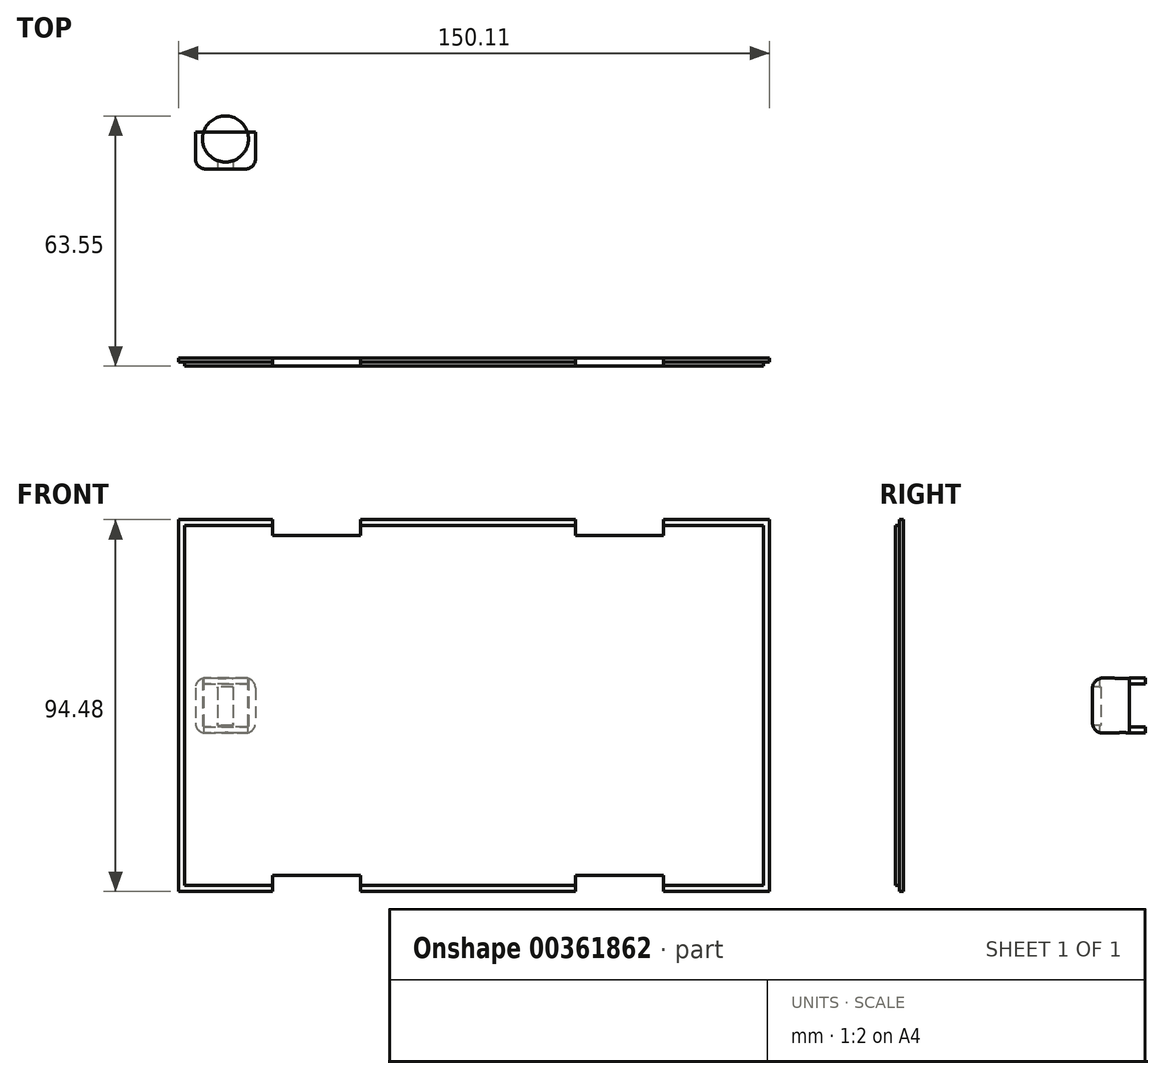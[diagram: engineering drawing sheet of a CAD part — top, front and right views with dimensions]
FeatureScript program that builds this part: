
annotation { "Feature Type Name" : "Feature", "Feature Type Description" : "" }
export const myFeature = defineFeature(function(context is Context, id is Id, definition is map)
    precondition{}
    {
        {
            var Q0;
            Q0=qCreatedBy(makeId("Front.planeOp"),FACE);
            var sketch = newSketch(context, id + "F0", { "sketchPlane" : qUnion([Q0])});
            skLineSegment(sketch, "E0", {"start": v(-53.36, 0) * mm, "end": v(-53.36, 45.72) * mm});
            skLineSegment(sketch, "E1", {"start": v(-53.36, 45.72) * mm, "end": v(-31, 45.72) * mm});
            skLineSegment(sketch, "E2", {"start": v(-31, 45.72) * mm, "end": v(-31, 43.18) * mm});
            skLineSegment(sketch, "E3", {"start": v(-31, 43.18) * mm, "end": v(-8.66, 43.18) * mm});
            skLineSegment(sketch, "E4", {"start": v(-8.66, 43.18) * mm, "end": v(-8.66, 45.72) * mm});
            skLineSegment(sketch, "E5", {"start": v(-8.66, 45.72) * mm, "end": v(45.95, 45.72) * mm});
            skLineSegment(sketch, "E6", {"start": v(45.95, 45.72) * mm, "end": v(45.95, 43.18) * mm});
            skLineSegment(sketch, "E7", {"start": v(45.95, 43.18) * mm, "end": v(68.3, 43.18) * mm});
            skLineSegment(sketch, "E8", {"start": v(68.3, 43.18) * mm, "end": v(68.3, 45.72) * mm});
            skLineSegment(sketch, "E9", {"start": v(68.3, 45.72) * mm, "end": v(93.7, 45.72) * mm});
            skLineSegment(sketch, "E10", {"start": v(93.7, 45.72) * mm, "end": v(93.7, 0) * mm});
            skLineSegment(sketch, "E11", {"start": v(93.7, 0) * mm, "end": v(-53.36, 0) * mm});
            skLineSegment(sketch, "E12.MirrorCS", {"start": v(-53.36, 0) * mm, "end": v(-53.36, -45.72) * mm});
            skLineSegment(sketch, "E13.MirrorCS", {"start": v(-53.36, -45.72) * mm, "end": v(-31, -45.72) * mm});
            skLineSegment(sketch, "E14.MirrorCS", {"start": v(-31, -45.72) * mm, "end": v(-31, -43.18) * mm});
            skLineSegment(sketch, "E15.MirrorCS", {"start": v(-31, -43.18) * mm, "end": v(-8.66, -43.18) * mm});
            skLineSegment(sketch, "E16.MirrorCS", {"start": v(-8.66, -43.18) * mm, "end": v(-8.66, -45.72) * mm});
            skLineSegment(sketch, "E17.MirrorCS", {"start": v(-8.66, -45.72) * mm, "end": v(45.95, -45.72) * mm});
            skLineSegment(sketch, "E18.MirrorCS", {"start": v(45.95, -45.72) * mm, "end": v(45.95, -43.18) * mm});
            skLineSegment(sketch, "E19.MirrorCS", {"start": v(45.95, -43.18) * mm, "end": v(68.3, -43.18) * mm});
            skLineSegment(sketch, "E20.MirrorCS", {"start": v(68.3, -43.18) * mm, "end": v(68.3, -45.72) * mm});
            skLineSegment(sketch, "E21.MirrorCS", {"start": v(68.3, -45.72) * mm, "end": v(93.7, -45.72) * mm});
            skLineSegment(sketch, "E22.MirrorCS", {"start": v(93.7, -45.72) * mm, "end": v(93.7, 0) * mm});
            skLineSegment(sketch, "E23.0", {"start": v(-54.88, 47.24) * mm, "end": v(-31, 47.24) * mm});
            skLineSegment(sketch, "E23.1", {"start": v(-54.88, 0) * mm, "end": v(-54.88, 47.24) * mm});
            skLineSegment(sketch, "E23.2", {"start": v(-54.88, 0) * mm, "end": v(-54.88, -47.24) * mm});
            skLineSegment(sketch, "E23.3", {"start": v(-54.88, -47.24) * mm, "end": v(-31, -47.24) * mm});
            skLineSegment(sketch, "E24", {"start": v(-31, 47.24) * mm, "end": v(-31, 45.72) * mm});
            skLineSegment(sketch, "E25", {"start": v(-31, -45.72) * mm, "end": v(-31, -47.24) * mm});
            skLineSegment(sketch, "E26", {"start": v(-8.66, 45.72) * mm, "end": v(-8.66, 47.24) * mm});
            skLineSegment(sketch, "E27", {"start": v(-8.66, 47.24) * mm, "end": v(45.95, 47.24) * mm});
            skLineSegment(sketch, "E28", {"start": v(45.95, 47.24) * mm, "end": v(45.95, 45.72) * mm});
            skLineSegment(sketch, "E29.0", {"start": v(68.3, -47.24) * mm, "end": v(95.23, -47.24) * mm});
            skLineSegment(sketch, "E29.1", {"start": v(95.23, -47.24) * mm, "end": v(95.23, 12.7) * mm});
            skLineSegment(sketch, "E29.2", {"start": v(95.23, 47.24) * mm, "end": v(95.23, 12.7) * mm});
            skLineSegment(sketch, "E29.3", {"start": v(68.3, 47.24) * mm, "end": v(95.23, 47.24) * mm});
            skLineSegment(sketch, "E30", {"start": v(68.3, 47.24) * mm, "end": v(68.3, 45.72) * mm});
            skLineSegment(sketch, "E31", {"start": v(68.3, -47.24) * mm, "end": v(68.3, -45.72) * mm});
            skLineSegment(sketch, "E32", {"start": v(-8.66, -45.72) * mm, "end": v(-8.66, -47.24) * mm});
            skLineSegment(sketch, "E33", {"start": v(-8.66, -47.24) * mm, "end": v(45.95, -47.24) * mm});
            skLineSegment(sketch, "E34", {"start": v(45.95, -47.24) * mm, "end": v(45.95, -45.72) * mm});
            skSolve(sketch);
        }
        {
            var Q0;
            Q0=makeQuery(id+"F0.imprint","IMPRINT",FACE,{"disambiguationData":[TD([[makeQuery(id+"F0.imprint","IMPRINT",EDGE,{"derivedFrom":sQuery(id+"F0.wireOp",EDGE,"E0")}),-1.0]])]});
            var Q1;
            Q1=makeQuery(id+"F0.imprint","IMPRINT",FACE,{"disambiguationData":[TD([[makeQuery(id+"F0.imprint","IMPRINT",EDGE,{"derivedFrom":sQuery(id+"F0.wireOp",EDGE,"E11")}),1.0]])]});
            extrude(context, id + "F1", {"entities" : qUnion([Q0, Q1]), "depth" : 2.03 * mm});
        }
        {
            var Q0;
            Q0=makeQuery(id+"F0.imprint","IMPRINT",FACE,{"disambiguationData":[TD([[makeQuery(id+"F0.imprint","IMPRINT",EDGE,{"derivedFrom":sQuery(id+"F0.wireOp",EDGE,"E0")}),1.0]])]});
            var Q1;
            Q1=makeQuery(id+"F0.imprint","IMPRINT",FACE,{"disambiguationData":[TD([[makeQuery(id+"F0.imprint","IMPRINT",EDGE,{"derivedFrom":sQuery(id+"F0.wireOp",EDGE,"E5")}),1.0]])]});
            var Q2;
            Q2=makeQuery(id+"F0.imprint","IMPRINT",FACE,{"disambiguationData":[TD([[makeQuery(id+"F0.imprint","IMPRINT",EDGE,{"derivedFrom":sQuery(id+"F0.wireOp",EDGE,"E9")}),1.0]])]});
            var Q3;
            Q3=makeQuery(id+"F0.imprint","IMPRINT",FACE,{"disambiguationData":[TD([[makeQuery(id+"F0.imprint","IMPRINT",EDGE,{"derivedFrom":sQuery(id+"F0.wireOp",EDGE,"E17.MirrorCS")}),-1.0]])]});
            extrude(context, id + "F2", {"entities" : qUnion([Q0, Q1, Q2, Q3]), "operationType" : NewBodyOperationType.ADD, "depth" : 1.02 * mm});
        }
        {
            var Q0;
            Q0=qCreatedBy(makeId("Top.planeOp"),FACE);
            var sketch = newSketch(context, id + "F3", { "sketchPlane" : qUnion([Q0])});
            skLineSegment(sketch, "E35.bottom", {"start": v(-50.6, 63.3) * mm, "end": v(-35.36, 63.3) * mm});
            skLineSegment(sketch, "E35.top", {"start": v(-50.6, 48.06) * mm, "end": v(-35.36, 48.06) * mm});
            skLineSegment(sketch, "E35.left", {"start": v(-50.6, 63.3) * mm, "end": v(-50.6, 48.06) * mm});
            skLineSegment(sketch, "E35.right", {"start": v(-35.36, 63.3) * mm, "end": v(-35.36, 48.06) * mm});
            skPoint(sketch, "E35.middle", {"position": v(-42.98, 55.68) * mm});
            skCircle(sketch, "E36", {"center": v(-42.98, 55.68) * mm, "radius": 5.84 * mm});
            skLineSegment(sketch, "E37", {"start": v(-50.6, 57.43) * mm, "end": v(-35.36, 57.43) * mm});
            skSolve(sketch);
        }
        {
            var Q0;
            {var subQ5=sQuery(id+"F3.wireOp",EDGE,"E35.top");Q0=makeQuery(id+"F3.imprint","IMPRINT",FACE,{"disambiguationData":[TD([[makeQuery(id+"F3.imprint","IMPRINT",EDGE,{"derivedFrom":subQ5}),1.0]])]});}
            var Q1;
            {var subQ0=sQuery(id+"F3.wireOp",EDGE,"E37");var subQ1=sQuery(id+"F3.wireOp",EDGE,"E36");var subQ2=makeQuery(id+"F3.imprint","INTERSECT",VERTEX,{"disambiguationData":[OD(0.0)],"derivedFrom":[subQ1,subQ0]});Q1=makeQuery(id+"F3.imprint","IMPRINT",FACE,{"disambiguationData":[TD([[makeQuery(id+"F3.imprint","IMPRINT",EDGE,{"disambiguationData":[TD([[subQ2,-1.0]])],"derivedFrom":subQ1}),1.0]])]});}
            extrude(context, id + "F4", {"entities" : qUnion([Q0, Q1]), "endBound" : BoundingType.SYMMETRIC, "depth" : 13.97 * mm});
        }
        {
            var Q0;
            {var subQ0=sQuery(id+"F3.wireOp",EDGE,"E37");var subQ1=sQuery(id+"F3.wireOp",EDGE,"E36");var subQ2=makeQuery(id+"F3.imprint","INTERSECT",VERTEX,{"disambiguationData":[OD(0.0)],"derivedFrom":[subQ1,subQ0]});Q0=makeQuery(id+"F3.imprint","IMPRINT",FACE,{"disambiguationData":[TD([[makeQuery(id+"F3.imprint","IMPRINT",EDGE,{"disambiguationData":[TD([[subQ2,-1.0]])],"derivedFrom":subQ1}),1.0]])]});}
            extrude(context, id + "F5", {"entities" : qUnion([Q0]), "operationType" : NewBodyOperationType.REMOVE, "endBound" : BoundingType.SYMMETRIC, "oppositeDirection" : true, "depth" : 10.92 * mm});
        }
        {
            var Q0;
            Q0=makeQuery(id+"F4.opExtrude","CAP_FACE",FACE,{"disambiguationData":[OSD([sQuery(id+"F3.wireOp",EDGE,"E35.top"),sQuery(id+"F3.wireOp",EDGE,"E35.left"),sQuery(id+"F3.wireOp",EDGE,"E35.right"),sQuery(id+"F3.wireOp",EDGE,"E37")])],"isStart":false});
            var sketch = newSketch(context, id + "F6", { "sketchPlane" : qUnion([Q0])});
            skCircle(sketch, "E38", {"center": v(-43.09, 53.26) * mm, "radius": 1.1 * mm});
            skSolve(sketch);
        }
        {
            var Q0;
            Q0=makeQuery(id+"F6.imprint","IMPRINT",FACE,{"disambiguationData":[TD([[makeQuery(id+"F6.imprint","IMPRINT",EDGE,{"derivedFrom":sQuery(id+"F6.wireOp",EDGE,"E38")}),1.0]])]});
            extrude(context, id + "F7", {"entities" : qUnion([Q0]), "operationType" : NewBodyOperationType.REMOVE, "oppositeDirection" : true, "depth" : 25.4 * mm});
        }
        {
            var Q0;
            Q0=makeQuery(id+"F4.opExtrude","SWEPT_FACE",FACE,{"disambiguationData":[OSD([sQuery(id+"F3.wireOp",EDGE,"E35.top")])]});
            var sketch = newSketch(context, id + "F8", { "sketchPlane" : qUnion([Q0])});
            skLineSegment(sketch, "E39.bottom", {"start": v(-44.95, 4.77) * mm, "end": v(-41.1, 4.77) * mm});
            skLineSegment(sketch, "E39.top", {"start": v(-44.95, -5.01) * mm, "end": v(-41.1, -5.01) * mm});
            skLineSegment(sketch, "E39.left", {"start": v(-44.95, 4.77) * mm, "end": v(-44.95, -5.01) * mm});
            skLineSegment(sketch, "E39.right", {"start": v(-41.1, 4.77) * mm, "end": v(-41.1, -5.01) * mm});
            skSolve(sketch);
        }
        {
            var Q0;
            Q0=makeQuery(id+"F8.imprint","IMPRINT",FACE,{"disambiguationData":[TD([[makeQuery(id+"F8.imprint","IMPRINT",EDGE,{"derivedFrom":sQuery(id+"F8.wireOp",EDGE,"E39.bottom")}),-1.0]])]});
            extrude(context, id + "F9", {"entities" : qUnion([Q0]), "operationType" : NewBodyOperationType.REMOVE, "oppositeDirection" : true, "depth" : 25.4 * mm});
        }
        {
            var Q0;
            Q0=makeQuery(id+"F4.opExtrude","CAP_EDGE",EDGE,{"disambiguationData":[OSD([sQuery(id+"F3.wireOp",EDGE,"E35.left")])],"isStart":false});
            var Q1;
            Q1=makeQuery(id+"F4.opExtrude","CAP_EDGE",EDGE,{"disambiguationData":[OSD([sQuery(id+"F3.wireOp",EDGE,"E35.left")])],"isStart":true});
            var Q2;
            Q2=makeQuery(id+"F4.opExtrude","CAP_EDGE",EDGE,{"disambiguationData":[OSD([sQuery(id+"F3.wireOp",EDGE,"E35.right")])],"isStart":false});
            var Q3;
            Q3=makeQuery(id+"F4.opExtrude","CAP_EDGE",EDGE,{"disambiguationData":[OSD([sQuery(id+"F3.wireOp",EDGE,"E35.right")])],"isStart":true});
            var Q4;
            Q4=makeQuery(id+"F4.opExtrude","SWEPT_EDGE",EDGE,{"disambiguationData":[OSD([sQuery(id+"F3.wireOp",EDGE,"E35.top"),sQuery(id+"F3.wireOp",EDGE,"E35.left")])]});
            var Q5;
            Q5=makeQuery(id+"F4.opExtrude","CAP_EDGE",EDGE,{"disambiguationData":[OSD([sQuery(id+"F3.wireOp",EDGE,"E35.top")])],"isStart":true});
            var Q6;
            Q6=makeQuery(id+"F4.opExtrude","SWEPT_EDGE",EDGE,{"disambiguationData":[OSD([sQuery(id+"F3.wireOp",EDGE,"E35.top"),sQuery(id+"F3.wireOp",EDGE,"E35.right")])]});
            var Q7;
            Q7=makeQuery(id+"F4.opExtrude","CAP_EDGE",EDGE,{"disambiguationData":[OSD([sQuery(id+"F3.wireOp",EDGE,"E35.top")])],"isStart":false});
            fillet(context, id + "F10", {"entities" : qUnion([Q0, Q1, Q2, Q3, Q4, Q5, Q6, Q7]), "radius" : 2.54 * mm, "tangentPropagation" : true, "allowEdgeOverflow" : false});
        }
    });
